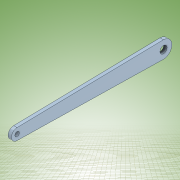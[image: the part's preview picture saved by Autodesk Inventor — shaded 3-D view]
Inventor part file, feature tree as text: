
AUTODESK INVENTOR PART (.ipt)
format: ipt  version: 2022 (Build 260153000, 153)  size: 122,368 bytes
history: native  units: mm
features: other x1, extrude x1, sketch x1
ambient origin geometry x8: Origin, YZ Plane, XZ Plane, XY Plane, X Axis, Y Axis, Z Axis, Center Point
bodies: Body1 (feature_tree)
feature tree (3):
  other  "Sólido1"
  extrude  "Extrusión1"  Depth=10.0mm
  sketch  "Boceto1"  dims[d0=4.0mm d1=10.0mm d2=6.35mm d3=130.0mm d4=15.0mm d5=3.0mm d6=0.0mm]
